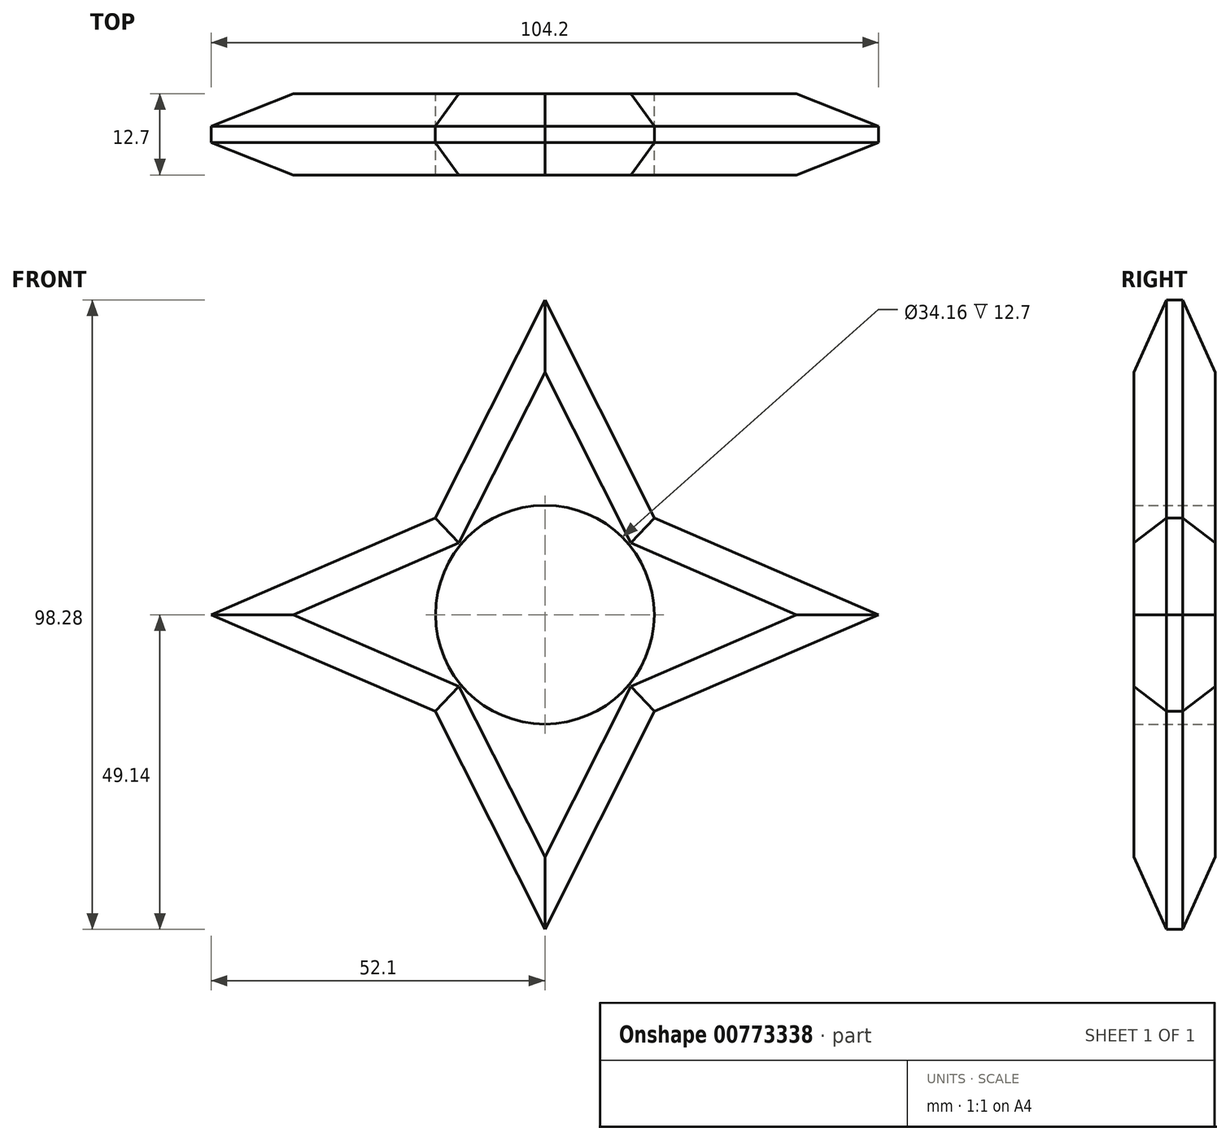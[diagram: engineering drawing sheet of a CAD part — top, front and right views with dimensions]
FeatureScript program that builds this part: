
annotation { "Feature Type Name" : "Feature", "Feature Type Description" : "" }
export const myFeature = defineFeature(function(context is Context, id is Id, definition is map)
    precondition{}
    {
        {
            var Q0;
            Q0=qCreatedBy(makeId("Front.planeOp"),FACE);
            var sketch = newSketch(context, id + "F0", { "sketchPlane" : qUnion([Q0])});
            skLineSegment(sketch, "E0", {"start": v(-52.1, 0) * mm, "end": v(-17.12, 15.1) * mm});
            skLineSegment(sketch, "E1", {"start": v(-17.12, 15.1) * mm, "end": v(0, 49.14) * mm});
            skLineSegment(sketch, "E2.MirrorCS", {"start": v(17.12, 15.1) * mm, "end": v(0, 49.14) * mm});
            skLineSegment(sketch, "E3.MirrorCS", {"start": v(52.1, 0) * mm, "end": v(17.12, 15.1) * mm});
            skLineSegment(sketch, "E4.MirrorCS", {"start": v(-52.1, 0) * mm, "end": v(-17.12, -15.1) * mm});
            skLineSegment(sketch, "E5.MirrorCS", {"start": v(-17.12, -15.1) * mm, "end": v(0, -49.14) * mm});
            skLineSegment(sketch, "E6.MirrorCS", {"start": v(17.12, -15.1) * mm, "end": v(0, -49.14) * mm});
            skLineSegment(sketch, "E7.MirrorCS", {"start": v(52.1, 0) * mm, "end": v(17.12, -15.1) * mm});
            skCircle(sketch, "E8", {"center": v(0, 0) * mm, "radius": 17.08 * mm});
            skSolve(sketch);
        }
        {
            var Q0;
            Q0 = qSketchRegion(id + "F0", true);
            extrude(context, id + "F1", {"entities" : qUnion([Q0]), "depth" : 12.7 * mm, "offsetDistance" : 25.4 * mm});
        }
        {
            var Q0;
            Q0=makeQuery(id+"F1.opExtrude","CAP_EDGE",EDGE,{"disambiguationData":[OSD([sQuery(id+"F0.wireOp",EDGE,"E4.MirrorCS")])],"isStart":false});
            var Q1;
            Q1=makeQuery(id+"F1.opExtrude","CAP_EDGE",EDGE,{"disambiguationData":[OSD([sQuery(id+"F0.wireOp",EDGE,"E0")])],"isStart":false});
            var Q2;
            Q2=makeQuery(id+"F1.opExtrude","CAP_EDGE",EDGE,{"disambiguationData":[OSD([sQuery(id+"F0.wireOp",EDGE,"E1")])],"isStart":false});
            var Q3;
            Q3=makeQuery(id+"F1.opExtrude","CAP_EDGE",EDGE,{"disambiguationData":[OSD([sQuery(id+"F0.wireOp",EDGE,"E2.MirrorCS")])],"isStart":false});
            var Q4;
            Q4=makeQuery(id+"F1.opExtrude","CAP_EDGE",EDGE,{"disambiguationData":[OSD([sQuery(id+"F0.wireOp",EDGE,"E3.MirrorCS")])],"isStart":false});
            var Q5;
            Q5=makeQuery(id+"F1.opExtrude","CAP_EDGE",EDGE,{"disambiguationData":[OSD([sQuery(id+"F0.wireOp",EDGE,"E7.MirrorCS")])],"isStart":false});
            var Q6;
            Q6=makeQuery(id+"F1.opExtrude","CAP_EDGE",EDGE,{"disambiguationData":[OSD([sQuery(id+"F0.wireOp",EDGE,"E6.MirrorCS")])],"isStart":false});
            var Q7;
            Q7=makeQuery(id+"F1.opExtrude","CAP_EDGE",EDGE,{"disambiguationData":[OSD([sQuery(id+"F0.wireOp",EDGE,"E5.MirrorCS")])],"isStart":false});
            chamfer(context, id + "F2", {"entities" : qUnion([Q0, Q1, Q2, Q3, Q4, Q5, Q6, Q7]), "width" : 5.08 * mm, "tangentPropagation" : true});
        }
        {
            var Q0;
            Q0=makeQuery(id+"F1.opExtrude","CAP_EDGE",EDGE,{"disambiguationData":[OSD([sQuery(id+"F0.wireOp",EDGE,"E2.MirrorCS")])],"isStart":true});
            var Q1;
            Q1=makeQuery(id+"F1.opExtrude","CAP_EDGE",EDGE,{"disambiguationData":[OSD([sQuery(id+"F0.wireOp",EDGE,"E1")])],"isStart":true});
            var Q2;
            Q2=makeQuery(id+"F1.opExtrude","CAP_EDGE",EDGE,{"disambiguationData":[OSD([sQuery(id+"F0.wireOp",EDGE,"E0")])],"isStart":true});
            var Q3;
            Q3=makeQuery(id+"F1.opExtrude","CAP_EDGE",EDGE,{"disambiguationData":[OSD([sQuery(id+"F0.wireOp",EDGE,"E4.MirrorCS")])],"isStart":true});
            var Q4;
            Q4=makeQuery(id+"F1.opExtrude","CAP_EDGE",EDGE,{"disambiguationData":[OSD([sQuery(id+"F0.wireOp",EDGE,"E5.MirrorCS")])],"isStart":true});
            var Q5;
            Q5=makeQuery(id+"F1.opExtrude","CAP_EDGE",EDGE,{"disambiguationData":[OSD([sQuery(id+"F0.wireOp",EDGE,"E6.MirrorCS")])],"isStart":true});
            var Q6;
            Q6=makeQuery(id+"F1.opExtrude","CAP_EDGE",EDGE,{"disambiguationData":[OSD([sQuery(id+"F0.wireOp",EDGE,"E7.MirrorCS")])],"isStart":true});
            var Q7;
            Q7=makeQuery(id+"F1.opExtrude","CAP_EDGE",EDGE,{"disambiguationData":[OSD([sQuery(id+"F0.wireOp",EDGE,"E3.MirrorCS")])],"isStart":true});
            chamfer(context, id + "F3", {"entities" : qUnion([Q0, Q1, Q2, Q3, Q4, Q5, Q6, Q7]), "width" : 5.08 * mm, "tangentPropagation" : true});
        }
    });
